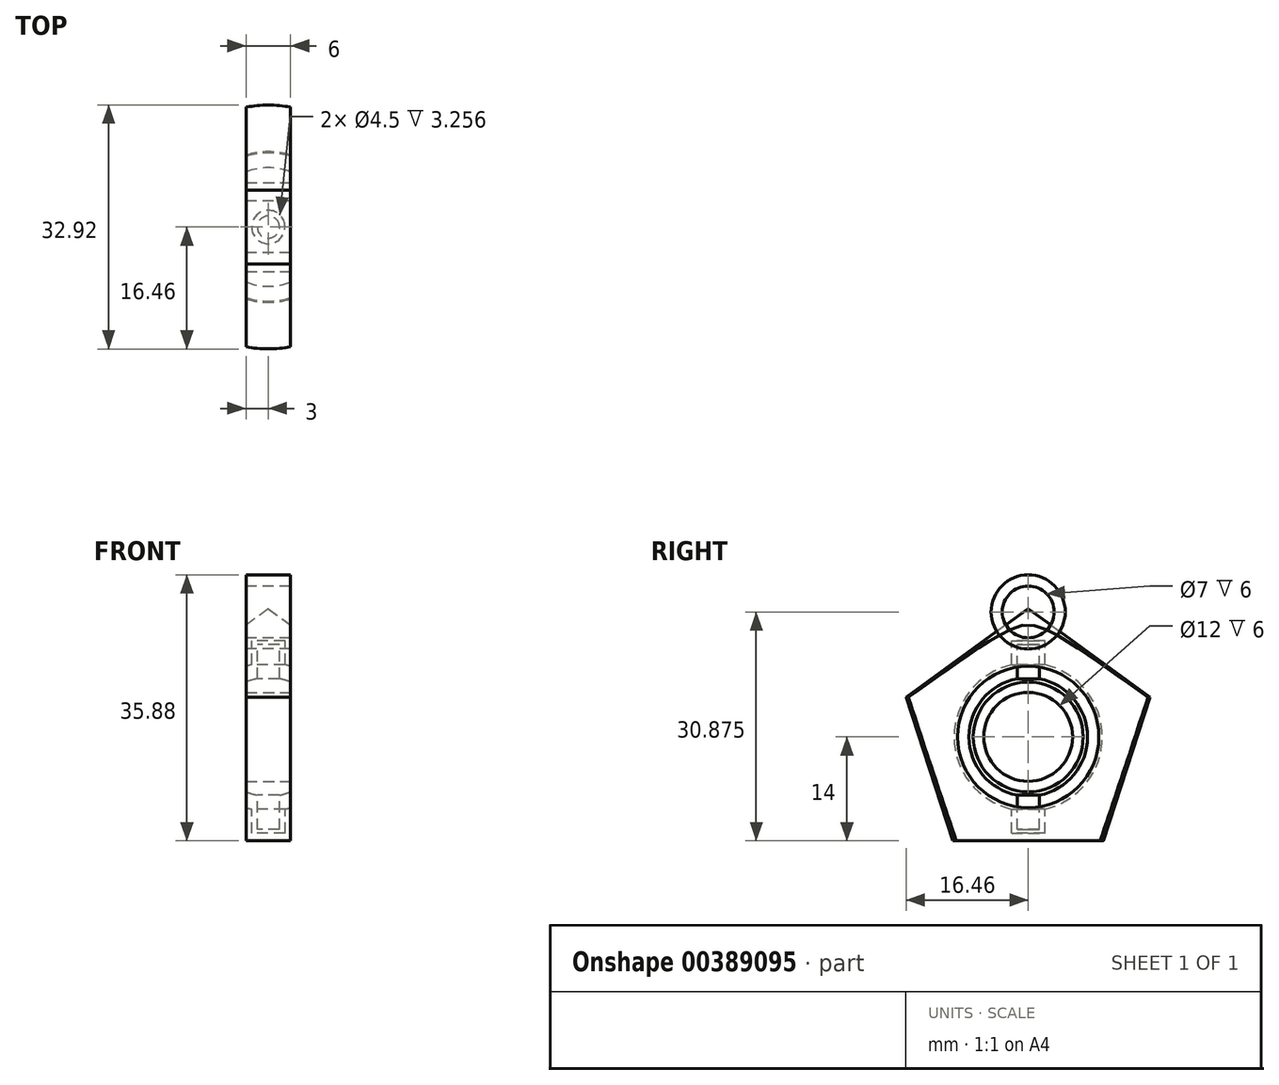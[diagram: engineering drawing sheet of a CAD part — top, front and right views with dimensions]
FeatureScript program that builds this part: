
annotation { "Feature Type Name" : "Feature", "Feature Type Description" : "" }
export const myFeature = defineFeature(function(context is Context, id is Id, definition is map)
    precondition{}
    {
        {
            var Q0;
            Q0=qCreatedBy(makeId("Front.planeOp"),FACE);
            var sketch = newSketch(context, id + "F0", { "sketchPlane" : qUnion([Q0])});
            skCircle(sketch, "E0.cCircle", {"center": v(0, 0) * mm, "radius": 14 * mm, "construction": true});
            skLineSegment(sketch, "E0.0", {"start": v(10.17, -14) * mm, "end": v(-10.17, -14) * mm});
            skLineSegment(sketch, "E0.1", {"start": v(-10.17, -14) * mm, "end": v(-16.46, 5.35) * mm});
            skLineSegment(sketch, "E0.2", {"start": v(-16.46, 5.35) * mm, "end": v(0, 17.3) * mm});
            skLineSegment(sketch, "E0.3", {"start": v(0, 17.3) * mm, "end": v(16.46, 5.35) * mm});
            skLineSegment(sketch, "E0.4", {"start": v(16.46, 5.35) * mm, "end": v(10.17, -14) * mm});
            skPoint(sketch, "E0.0.midPoint", {"position": v(0, -14) * mm});
            skArc(sketch, "E1", {"start": v(-2.25, 9.74) * mm, "mid": v(-10, 0) * mm, "end": v(-2.25, -9.74) * mm});
            skArc(sketch, "E2", {"start": v(1.5, -7.86) * mm, "mid": v(8, 0) * mm, "end": v(1.5, 7.86) * mm});
            skLineSegment(sketch, "E3.bottom", {"start": v(1.5, -12.5) * mm, "end": v(-1.5, -12.5) * mm});
            skLineSegment(sketch, "E3.top", {"start": v(1.5, 12.5) * mm, "end": v(-1.5, 12.5) * mm});
            skLineSegment(sketch, "E3.left", {"start": v(1.5, -12.5) * mm, "end": v(1.5, -7.86) * mm});
            skLineSegment(sketch, "E3.right", {"start": v(-1.5, -12.5) * mm, "end": v(-1.5, -7.86) * mm});
            skLineSegment(sketch, "E4.bottom", {"start": v(2.25, -13) * mm, "end": v(-2.25, -13) * mm});
            skLineSegment(sketch, "E4.top", {"start": v(2.25, 13) * mm, "end": v(-2.25, 13) * mm});
            skLineSegment(sketch, "E4.left", {"start": v(2.25, -13) * mm, "end": v(2.25, -9.74) * mm});
            skLineSegment(sketch, "E4.right", {"start": v(-2.25, -13) * mm, "end": v(-2.25, -9.74) * mm});
            skLineSegment(sketch, "E5.trimOffspring", {"start": v(-2.25, 9.74) * mm, "end": v(-2.25, 13) * mm});
            skLineSegment(sketch, "E6.trimOffspring", {"start": v(2.25, 9.74) * mm, "end": v(2.25, 13) * mm});
            skLineSegment(sketch, "E7.trimOffspring", {"start": v(-1.5, 7.86) * mm, "end": v(-1.5, 12.5) * mm});
            skLineSegment(sketch, "E8.trimOffspring", {"start": v(1.5, 7.86) * mm, "end": v(1.5, 12.5) * mm});
            skArc(sketch, "E9.trimOffspring", {"start": v(-1.5, 7.86) * mm, "mid": v(-8, 0) * mm, "end": v(-1.5, -7.86) * mm});
            skArc(sketch, "E10.trimOffspring", {"start": v(2.25, -9.74) * mm, "mid": v(10, 0) * mm, "end": v(2.25, 9.74) * mm});
            skLineSegment(sketch, "E11", {"start": v(0, 17.3) * mm, "end": v(0, -14) * mm});
            skSolve(sketch);
        }
        {
            var Q0;
            {var subQ4=sQuery(id+"F0.wireOp",EDGE,"E3.right");Q0=makeQuery(id+"F0.imprint","IMPRINT",FACE,{"disambiguationData":[TD([[makeQuery(id+"F0.imprint","IMPRINT",EDGE,{"derivedFrom":subQ4}),-1.0]])]});}
            var Q1;
            {var subQ1=sQuery(id+"F0.wireOp",EDGE,"E0.1");Q1=makeQuery(id+"F0.imprint","IMPRINT",FACE,{"disambiguationData":[TD([[makeQuery(id+"F0.imprint","IMPRINT",EDGE,{"derivedFrom":subQ1}),-1.0]])]});}
            var Q2;
            Q2=sQuery(id+"F0.wireOp",EDGE,"E11");
            revolve(context, id + "F1", {"entities" : qUnion([Q0, Q1]), "axis" : qUnion([Q2]), "revolveType" : RevolveType.FULL});
        }
        {
            var Q0;
            Q0=qCreatedBy(makeId("Front.planeOp"),FACE);
            var sketch = newSketch(context, id + "F2", { "sketchPlane" : qUnion([Q0])});
            skLineSegment(sketch, "E12.bottom", {"start": v(3, -45.07) * mm, "end": v(-3, -45.07) * mm});
            skLineSegment(sketch, "E12.top", {"start": v(3, 45.07) * mm, "end": v(-3, 45.07) * mm});
            skLineSegment(sketch, "E12.left", {"start": v(3, -45.07) * mm, "end": v(3, 45.07) * mm});
            skLineSegment(sketch, "E12.right", {"start": v(-3, -45.07) * mm, "end": v(-3, 45.07) * mm});
            skPoint(sketch, "E12.middle", {"position": v(0, 0) * mm});
            skSolve(sketch);
        }
        {
            var Q0;
            Q0 = qSketchRegion(id + "F2", true);
            extrude(context, id + "F3", {"entities" : qUnion([Q0]), "operationType" : NewBodyOperationType.INTERSECT, "endBound" : BoundingType.SYMMETRIC, "depth" : 40 * mm});
        }
        {
            var Q0;
            Q0=qCreatedBy(makeId("Right.planeOp"),FACE);
            var sketch = newSketch(context, id + "F4", { "sketchPlane" : qUnion([Q0])});
            skCircle(sketch, "E13", {"center": v(0, 16.88) * mm, "radius": 3.5 * mm});
            skCircle(sketch, "E14", {"center": v(0, 16.88) * mm, "radius": 5 * mm});
            skSolve(sketch);
        }
        {
            var Q0;
            Q0=makeQuery(id+"F4.imprint","IMPRINT",FACE,{"disambiguationData":[TD([[makeQuery(id+"F4.imprint","IMPRINT",EDGE,{"derivedFrom":sQuery(id+"F4.wireOp",EDGE,"E13")}),-1.0]])]});
            extrude(context, id + "F5", {"entities" : qUnion([Q0]), "endBound" : BoundingType.SYMMETRIC, "depth" : 6 * mm});
        }
        {
            var Q0;
            Q0=qCreatedBy(makeId("Right.planeOp"),FACE);
            var sketch = newSketch(context, id + "F6", { "sketchPlane" : qUnion([Q0])});
            skCircle(sketch, "E15", {"center": v(0, 0) * mm, "radius": 6 * mm});
            skSolve(sketch);
        }
        {
            var Q0;
            Q0 = qSketchRegion(id + "F6", true);
            extrude(context, id + "F7", {"entities" : qUnion([Q0]), "operationType" : NewBodyOperationType.REMOVE, "endBound" : BoundingType.SYMMETRIC, "oppositeDirection" : true, "depth" : 6 * mm});
        }
    });
